# Revit family: PRD_FrankeWS_WCPans_HEAVY-DUTY_HDTX592,594
name_source: partatom
category: Plumbing Fixtures
revit_build: Autodesk Revit 2018 (Build: 20190510_1515(x64)
units: mm (PartAtom-declared; Revit-internal decimal feet)

## family parameters
Cut with Voids When Loaded = No
Host = Face
OmniClass Number = 23.45.05.21.11.21
OmniClass Title = Urinals
Part Type = Normal
Room Calculation Point = No
Round Connector Dimension = Use Diameter
Shared = No

## types (2) — shared parameters
AssetType = Fixed
Category = Pr_40_20_93_94, WC pans
Default Elevation = 500 mm  [stored 1.64042 ft]
DurationUnit = year
Finish = Satin finished
Form = WALL-HUNG
IfcExportAs = IfcSanitaryTerminalType
IfcExportType = TOILETPAN
InletSize = 55  [stored 0.180446 ft]
IntegralAccessories = Includes Mounting material
Manufacturer = KWC Group AG
ManufacturerName = KWC Group AG
ManufacturerURL = www.kwc.com
Material = PRD_AR_StainlessSteel_SatinFinished
MaterialsBody = Stainless steel
MaterialsFinishAndColour = Stainless steel
MinimumFlushingCapacity = 4.00 l
NBSDescription = WC pans
NBSReference = 45-35-70/384
NominalDepth = 351 mm  [stored 1.15157 ft]
NominalHeight = 351 mm  [stored 1.15157 ft]
NominalWidth = 360 mm  [stored 1.1811 ft]
PanColor = Stainless steel
PanMaterial = Stainless steel
PanMounting = WallHung
ProductInformation = https://pim.kwc.com
SpilloverLevel = 400 mm  [stored 1.31234 ft]
ToiletPanType = Other
ToiletType = LooseCoupled
URL = www.kwc.com
Uniclass2015Code = Pr_40_20_93_94
Uniclass2015Title = WC pans
Uniclass2015Version = Products v1.7
Version = 1
WarrantyDurationUnit = year
WasteSize = 100  [stored 0.328084 ft]

## per-type parameters (varying)
| type | BIMObjectName | Description | Features | GrossWeight | ModelNumber | Name | NetWeight | NominalLength | Size |
| HDTX594 | PRD_AR_WCPans_HEAVY-DUTY_HDTX594 | Wall hung WC pan for disabled, hidden mounting with stainless steel rods through wall, fixing and service via maintenance room, stainless steel, surface satin finished, material thickness 1.6 mm, flushing certificated to EN 997, concealed flushing rim with min. 4 liter flushing capacity, with a shrouded 100 mm diameter horiziontal 'P' trap outlet, pressed seat area tapered towards centre, all edges curved, fixing with 280 mm stainless steel rods and screw nuts (included) through the wall. | stainless steel, 1.60 mm, satin finished, bolt fix with duct wall, 360x351x700 mm (WxHxD) | 18.25 kg | 2000100444 | HEAVY-DUTY WC HDTX594 | 17.34 kg | 700 mm  [stored 2.29659 ft] | 360 x 351 x 700 mm |
| HDTX592 | PRD_AR_WCPans_HEAVY-DUTY_HDTX592 | Wall hung WC pan, hidden mounting with stainless steel rods through wall, fixing and service via maintenance room, stainless steel, surface satin finished, material thickness 1.6 mm, flushing certificated to EN 997, concealed flushing rim with min. 4 liter flushing capacity, with a shrouded 100 mm diameter horizontal 'P' trap outlet, pressed seat area tapered towards centre, all edges curved, fixing with 280 mm stainless steel rods and screw nuts (included) through the wall. 4 litre flush EN997 approved. Products can be foam filled, on request, for extra strength and reduction of noise in a security environment. Without seat and lid. | stainless steel, 1.60 mm, satin finished, bolt fix with duct wall, 360x351x500 mm (WxHxD) | 15.90 kg | 2000100447 | HEAVY-DUTY WC HDTX592 | 13.74 kg | 500 mm  [stored 1.64042 ft] | 360 x 351 x 500 mm |

note: column(s) folded — value = type name in every type: Model, ModelReference, Type

note: [stored X ft] marks values corroborated as IEEE doubles in the binary element streams (Revit-internal decimal feet)

## geometry (parser evidence)
native form markers: Sweep x5
no freeform markers — native parametric forms only
